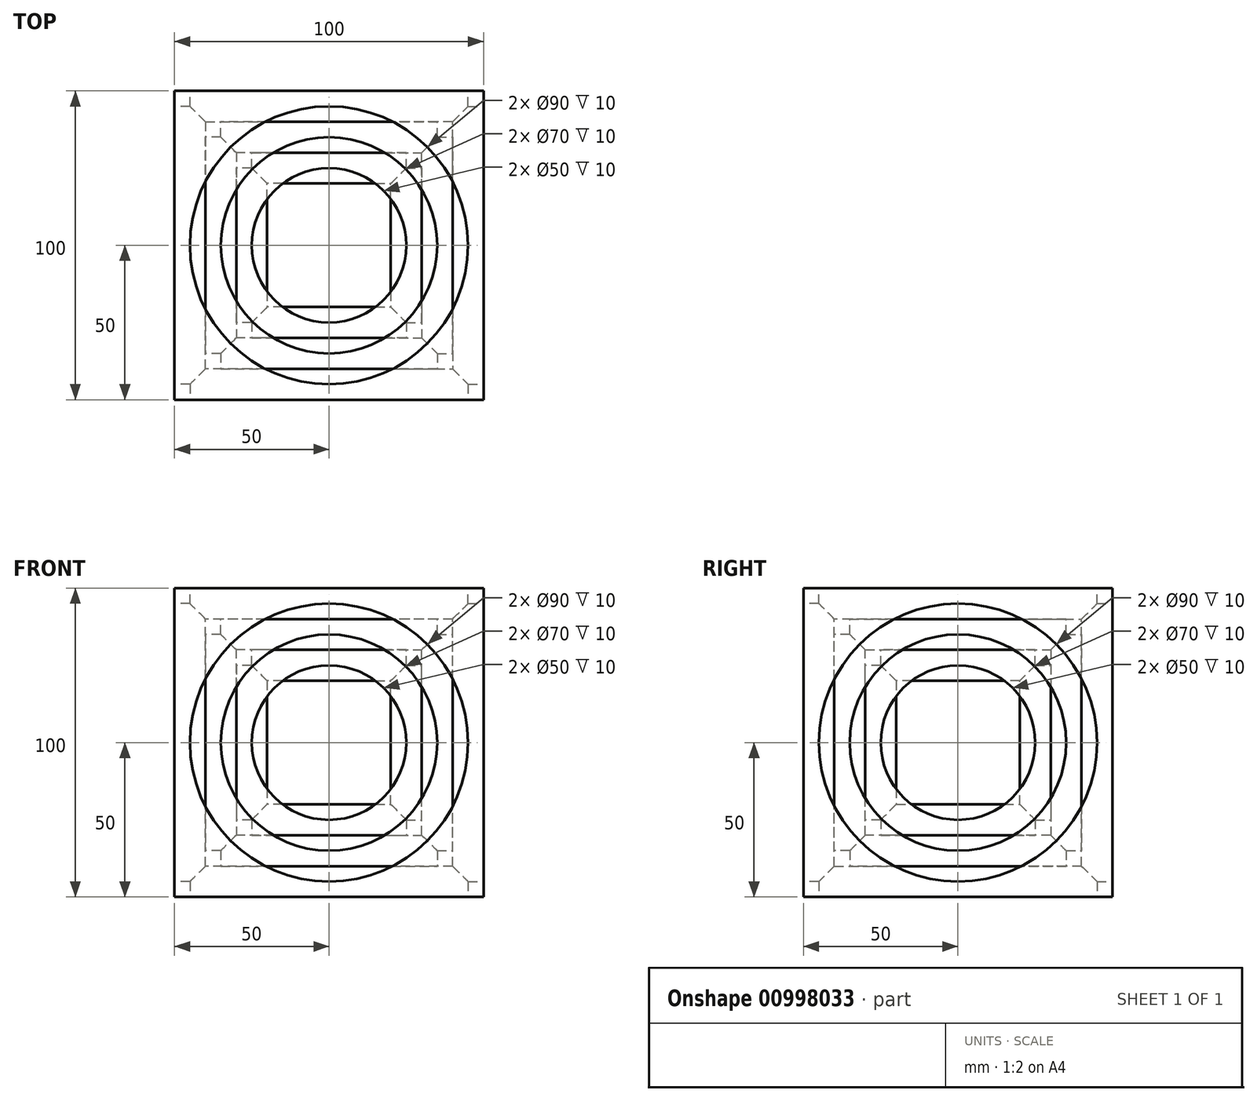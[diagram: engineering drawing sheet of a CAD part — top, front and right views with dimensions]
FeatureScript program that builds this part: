
annotation { "Feature Type Name" : "Feature", "Feature Type Description" : "" }
export const myFeature = defineFeature(function(context is Context, id is Id, definition is map)
    precondition{}
    {
        {
            assignVariable(context, id + "F0", {"name" : "W", "anyValue" : 100});
        }
        {
            assignVariable(context, id + "F1", {"name" : "S", "anyValue" : 10});
        }
        {
            var Q0;
            Q0=qCreatedBy(makeId("Top.planeOp"),FACE);
            var sketch = newSketch(context, id + "F2", { "sketchPlane" : qUnion([Q0])});
            skLineSegment(sketch, "E0.bottom", {"start": v(50, -50) * mm, "end": v(-50, -50) * mm});
            skLineSegment(sketch, "E0.top", {"start": v(50, 50) * mm, "end": v(-50, 50) * mm});
            skLineSegment(sketch, "E0.left", {"start": v(50, -50) * mm, "end": v(50, 50) * mm});
            skLineSegment(sketch, "E0.right", {"start": v(-50, -50) * mm, "end": v(-50, 50) * mm});
            skPoint(sketch, "E0.middle", {"position": v(0, 0) * mm});
            skSolve(sketch);
        }
        {
            var Q0;
            Q0=makeQuery(id+"F2.imprint","IMPRINT",FACE,{"disambiguationData":[TD([[makeQuery(id+"F2.imprint","IMPRINT",EDGE,{"derivedFrom":sQuery(id+"F2.wireOp",EDGE,"E0.bottom")}),-1.0]])]});
            extrude(context, id + "F3", {"entities" : qUnion([Q0]), "depth" : (getVariable(context, 'W') / 2) * mm, "offsetDistance" : 25 * mm, "hasSecondDirection" : true, "secondDirectionOppositeDirection" : true, "secondDirectionDepth" : (getVariable(context, 'W') / 2) * mm});
        }
        {
            var Q0;
            Q0=qCreatedBy(makeId("Front.planeOp"),FACE);
            cPlane(context, id + "F4", {"entities" : qUnion([Q0]), "cplaneType" : CPlaneType.OFFSET, "offset" : (getVariable(context, 'W') / 2) * mm, "width" : 150 * mm, "height" : 150 * mm});
        }
        {
            var Q0;
            Q0=qCreatedBy(id+"F4.planeOp",FACE);
            var sketch = newSketch(context, id + "F5", { "sketchPlane" : qUnion([Q0])});
            skCircle(sketch, "E1", {"center": v(0, 0) * mm, "radius": 45 * mm});
            skSolve(sketch);
        }
        {
            var Q0;
            Q0=makeQuery(id+"F5.imprint","IMPRINT",FACE,{"disambiguationData":[TD([[makeQuery(id+"F5.imprint","IMPRINT",EDGE,{"derivedFrom":sQuery(id+"F5.wireOp",EDGE,"E1")}),1.0]])]});
            extrude(context, id + "F6", {"entities" : qUnion([Q0]), "operationType" : NewBodyOperationType.REMOVE, "oppositeDirection" : true, "depth" : (getVariable(context, 'S')) * mm, "offsetDistance" : 25 * mm});
        }
        {
            var Q0;
            Q0=qCreatedBy(makeId("Right.planeOp"),FACE);
            cPlane(context, id + "F7", {"entities" : qUnion([Q0]), "cplaneType" : CPlaneType.OFFSET, "offset" : (getVariable(context, 'W') / 2) * mm, "width" : 150 * mm, "height" : 150 * mm});
        }
        {
            var Q0;
            Q0=qCreatedBy(id+"F7.planeOp",FACE);
            var sketch = newSketch(context, id + "F8", { "sketchPlane" : qUnion([Q0])});
            skCircle(sketch, "E2", {"center": v(0, 0) * mm, "radius": 45 * mm});
            skSolve(sketch);
        }
        {
            var Q0;
            Q0=makeQuery(id+"F8.imprint","IMPRINT",FACE,{"disambiguationData":[TD([[makeQuery(id+"F8.imprint","IMPRINT",EDGE,{"derivedFrom":sQuery(id+"F8.wireOp",EDGE,"E2")}),1.0]])]});
            extrude(context, id + "F9", {"entities" : qUnion([Q0]), "operationType" : NewBodyOperationType.REMOVE, "oppositeDirection" : true, "depth" : (getVariable(context, 'S')) * mm, "offsetDistance" : 25 * mm});
        }
        {
            var Q0;
            Q0=qCreatedBy(makeId("Top.planeOp"),FACE);
            cPlane(context, id + "F10", {"entities" : qUnion([Q0]), "cplaneType" : CPlaneType.OFFSET, "offset" : (getVariable(context, 'W') / 2) * mm, "width" : 150 * mm, "height" : 150 * mm});
        }
        {
            var Q0;
            Q0=qCreatedBy(id+"F10.planeOp",FACE);
            var sketch = newSketch(context, id + "F11", { "sketchPlane" : qUnion([Q0])});
            skCircle(sketch, "E3", {"center": v(0, 0) * mm, "radius": 45 * mm});
            skSolve(sketch);
        }
        {
            var Q0;
            Q0=makeQuery(id+"F11.imprint","IMPRINT",FACE,{"disambiguationData":[TD([[makeQuery(id+"F11.imprint","IMPRINT",EDGE,{"derivedFrom":sQuery(id+"F11.wireOp",EDGE,"E3")}),1.0]])]});
            extrude(context, id + "F12", {"entities" : qUnion([Q0]), "operationType" : NewBodyOperationType.REMOVE, "oppositeDirection" : true, "depth" : (getVariable(context, 'S')) * mm, "offsetDistance" : 25 * mm});
        }
        {
            var Q0;
            Q0=qCreatedBy(makeId("Top.planeOp"),FACE);
            cPlane(context, id + "F13", {"entities" : qUnion([Q0]), "cplaneType" : CPlaneType.OFFSET, "offset" : (getVariable(context, 'W') / 2) * mm, "oppositeDirection" : true, "width" : 150 * mm, "height" : 150 * mm});
        }
        {
            var Q0;
            Q0=qCreatedBy(id+"F13.planeOp",FACE);
            var sketch = newSketch(context, id + "F14", { "sketchPlane" : qUnion([Q0])});
            skCircle(sketch, "E4", {"center": v(0, 0) * mm, "radius": 45 * mm});
            skSolve(sketch);
        }
        {
            var Q0;
            Q0 = qSketchRegion(id + "F14", true);
            extrude(context, id + "F15", {"entities" : qUnion([Q0]), "operationType" : NewBodyOperationType.REMOVE, "oppositeDirection" : true, "depth" : (-getVariable(context, 'S')) * mm, "offsetDistance" : 25 * mm});
        }
        {
            var Q0;
            Q0=qCreatedBy(makeId("Front.planeOp"),FACE);
            cPlane(context, id + "F16", {"entities" : qUnion([Q0]), "cplaneType" : CPlaneType.OFFSET, "offset" : (getVariable(context, 'W') / 2) * mm, "oppositeDirection" : true, "width" : 150 * mm, "height" : 150 * mm});
        }
        {
            var Q0;
            Q0=qCreatedBy(id+"F16.planeOp",FACE);
            var sketch = newSketch(context, id + "F17", { "sketchPlane" : qUnion([Q0])});
            skCircle(sketch, "E5", {"center": v(0, 0) * mm, "radius": 45 * mm});
            skSolve(sketch);
        }
        {
            var Q0;
            Q0=makeQuery(id+"F17.imprint","IMPRINT",FACE,{"disambiguationData":[TD([[makeQuery(id+"F17.imprint","IMPRINT",EDGE,{"derivedFrom":sQuery(id+"F17.wireOp",EDGE,"E5")}),1.0]])]});
            extrude(context, id + "F18", {"entities" : qUnion([Q0]), "operationType" : NewBodyOperationType.REMOVE, "oppositeDirection" : true, "depth" : (-getVariable(context, 'S')) * mm, "offsetDistance" : 25 * mm});
        }
        {
            var Q0;
            Q0=qCreatedBy(makeId("Right.planeOp"),FACE);
            cPlane(context, id + "F19", {"entities" : qUnion([Q0]), "cplaneType" : CPlaneType.OFFSET, "offset" : (getVariable(context, 'W') / 2) * mm, "oppositeDirection" : true, "width" : 150 * mm, "height" : 150 * mm});
        }
        {
            var Q0;
            Q0=qCreatedBy(id+"F19.planeOp",FACE);
            var sketch = newSketch(context, id + "F20", { "sketchPlane" : qUnion([Q0])});
            skCircle(sketch, "E6", {"center": v(0, 0) * mm, "radius": 45 * mm});
            skSolve(sketch);
        }
        {
            var Q0;
            Q0=makeQuery(id+"F20.imprint","IMPRINT",FACE,{"disambiguationData":[TD([[makeQuery(id+"F20.imprint","IMPRINT",EDGE,{"derivedFrom":sQuery(id+"F20.wireOp",EDGE,"E6")}),1.0]])]});
            extrude(context, id + "F21", {"entities" : qUnion([Q0]), "operationType" : NewBodyOperationType.REMOVE, "oppositeDirection" : true, "depth" : (-getVariable(context, 'S')) * mm, "offsetDistance" : 25 * mm});
        }
        {
            var Q0;
            Q0=makeQuery(id+"F21.boolean.opBoolean","COPY",FACE,{"derivedFrom":makeQuery(id+"F21.opExtrude","CAP_FACE",FACE,{"disambiguationData":[OSD([sQuery(id+"F20.wireOp",EDGE,"E6")])],"isStart":false})});
            var sketch = newSketch(context, id + "F22", { "sketchPlane" : qUnion([Q0])});
            skLineSegment(sketch, "E7", {"start": v(0, 40) * mm, "end": v(0, -40) * mm, "construction": true});
            skCircle(sketch, "E8", {"center": v(0, 0) * mm, "radius": 35 * mm});
            skSolve(sketch);
        }
        {
            var Q0;
            Q0=makeQuery(id+"F22.imprint","IMPRINT",FACE,{"disambiguationData":[TD([[makeQuery(id+"F22.imprint","IMPRINT",EDGE,{"derivedFrom":sQuery(id+"F22.wireOp",EDGE,"E8")}),1.0]])]});
            extrude(context, id + "F23", {"entities" : qUnion([Q0]), "operationType" : NewBodyOperationType.REMOVE, "oppositeDirection" : true, "depth" : (getVariable(context, 'S')) * mm, "offsetDistance" : 25 * mm});
        }
        {
            var Q0;
            Q0=makeQuery(id+"F6.boolean.opBoolean","COPY",FACE,{"derivedFrom":makeQuery(id+"F6.opExtrude","CAP_FACE",FACE,{"disambiguationData":[OSD([sQuery(id+"F5.wireOp",EDGE,"E1")])],"isStart":false})});
            var sketch = newSketch(context, id + "F24", { "sketchPlane" : qUnion([Q0])});
            skLineSegment(sketch, "E9", {"start": v(0, 24.49) * mm, "end": v(0, -24.49) * mm, "construction": true});
            skCircle(sketch, "E10", {"center": v(0, 0) * mm, "radius": 35 * mm});
            skSolve(sketch);
        }
        {
            var Q0;
            Q0=makeQuery(id+"F24.imprint","IMPRINT",FACE,{"disambiguationData":[TD([[makeQuery(id+"F24.imprint","IMPRINT",EDGE,{"derivedFrom":sQuery(id+"F24.wireOp",EDGE,"E10")}),1.0]])]});
            extrude(context, id + "F25", {"entities" : qUnion([Q0]), "operationType" : NewBodyOperationType.REMOVE, "oppositeDirection" : true, "depth" : (getVariable(context, 'S')) * mm, "offsetDistance" : 25 * mm});
        }
        {
            var Q0;
            Q0=makeQuery(id+"F12.boolean.opBoolean","COPY",FACE,{"derivedFrom":makeQuery(id+"F12.opExtrude","CAP_FACE",FACE,{"disambiguationData":[OSD([sQuery(id+"F11.wireOp",EDGE,"E3")])],"isStart":false})});
            var sketch = newSketch(context, id + "F26", { "sketchPlane" : qUnion([Q0])});
            skLineSegment(sketch, "E11", {"start": v(0, 24.49) * mm, "end": v(0, -24.49) * mm, "construction": true});
            skCircle(sketch, "E12", {"center": v(0, 0) * mm, "radius": 35 * mm});
            skSolve(sketch);
        }
        {
            var Q0;
            Q0=makeQuery(id+"F26.imprint","IMPRINT",FACE,{"disambiguationData":[TD([[makeQuery(id+"F26.imprint","IMPRINT",EDGE,{"derivedFrom":sQuery(id+"F26.wireOp",EDGE,"E12")}),1.0]])]});
            extrude(context, id + "F27", {"entities" : qUnion([Q0]), "operationType" : NewBodyOperationType.REMOVE, "oppositeDirection" : true, "depth" : (getVariable(context, 'S')) * mm, "offsetDistance" : 25 * mm});
        }
        {
            var Q0;
            Q0=makeQuery(id+"F18.boolean.opBoolean","COPY",FACE,{"derivedFrom":makeQuery(id+"F18.opExtrude","CAP_FACE",FACE,{"disambiguationData":[OSD([sQuery(id+"F17.wireOp",EDGE,"E5")])],"isStart":false})});
            var sketch = newSketch(context, id + "F28", { "sketchPlane" : qUnion([Q0])});
            skLineSegment(sketch, "E13", {"start": v(0, 24.49) * mm, "end": v(0, -24.49) * mm, "construction": true});
            skCircle(sketch, "E14", {"center": v(0, 0) * mm, "radius": 35 * mm});
            skSolve(sketch);
        }
        {
            var Q0;
            Q0=makeQuery(id+"F28.imprint","IMPRINT",FACE,{"disambiguationData":[TD([[makeQuery(id+"F28.imprint","IMPRINT",EDGE,{"derivedFrom":sQuery(id+"F28.wireOp",EDGE,"E14")}),1.0]])]});
            extrude(context, id + "F29", {"entities" : qUnion([Q0]), "operationType" : NewBodyOperationType.REMOVE, "oppositeDirection" : true, "depth" : (getVariable(context, 'S')) * mm, "offsetDistance" : 25 * mm});
        }
        {
            var Q0;
            Q0=makeQuery(id+"F15.boolean.opBoolean","COPY",FACE,{"derivedFrom":makeQuery(id+"F15.opExtrude","CAP_FACE",FACE,{"disambiguationData":[OSD([sQuery(id+"F14.wireOp",EDGE,"E4")])],"isStart":false})});
            var sketch = newSketch(context, id + "F30", { "sketchPlane" : qUnion([Q0])});
            skLineSegment(sketch, "E15", {"start": v(0, 24.49) * mm, "end": v(0, -24.49) * mm, "construction": true});
            skCircle(sketch, "E16", {"center": v(0, 0) * mm, "radius": 35 * mm});
            skSolve(sketch);
        }
        {
            var Q0;
            Q0=makeQuery(id+"F30.imprint","IMPRINT",FACE,{"disambiguationData":[TD([[makeQuery(id+"F30.imprint","IMPRINT",EDGE,{"derivedFrom":sQuery(id+"F30.wireOp",EDGE,"E16")}),1.0]])]});
            extrude(context, id + "F31", {"entities" : qUnion([Q0]), "operationType" : NewBodyOperationType.REMOVE, "oppositeDirection" : true, "depth" : (getVariable(context, 'S')) * mm, "offsetDistance" : 25 * mm});
        }
        {
            var Q0;
            Q0=makeQuery(id+"F9.boolean.opBoolean","COPY",FACE,{"derivedFrom":makeQuery(id+"F9.opExtrude","CAP_FACE",FACE,{"disambiguationData":[OSD([sQuery(id+"F8.wireOp",EDGE,"E2")])],"isStart":false})});
            var sketch = newSketch(context, id + "F32", { "sketchPlane" : qUnion([Q0])});
            skLineSegment(sketch, "E17", {"start": v(0, 24.49) * mm, "end": v(0, -24.49) * mm, "construction": true});
            skCircle(sketch, "E18", {"center": v(0, 0) * mm, "radius": 35 * mm});
            skSolve(sketch);
        }
        {
            var Q0;
            Q0=makeQuery(id+"F32.imprint","IMPRINT",FACE,{"disambiguationData":[TD([[makeQuery(id+"F32.imprint","IMPRINT",EDGE,{"derivedFrom":sQuery(id+"F32.wireOp",EDGE,"E18")}),1.0]])]});
            extrude(context, id + "F33", {"entities" : qUnion([Q0]), "operationType" : NewBodyOperationType.REMOVE, "oppositeDirection" : true, "depth" : (getVariable(context, 'S')) * mm, "offsetDistance" : 25 * mm});
        }
        {
            var Q0;
            Q0=makeQuery(id+"F25.boolean.opBoolean","COPY",FACE,{"derivedFrom":makeQuery(id+"F25.opExtrude","CAP_FACE",FACE,{"disambiguationData":[OSD([sQuery(id+"F24.wireOp",EDGE,"E10")])],"isStart":false})});
            var sketch = newSketch(context, id + "F34", { "sketchPlane" : qUnion([Q0])});
            skLineSegment(sketch, "E19", {"start": v(0, 15.6) * mm, "end": v(0, -15.6) * mm, "construction": true});
            skCircle(sketch, "E20", {"center": v(0, 0) * mm, "radius": 25 * mm});
            skSolve(sketch);
        }
        {
            var Q0;
            Q0=makeQuery(id+"F34.imprint","IMPRINT",FACE,{"disambiguationData":[TD([[makeQuery(id+"F34.imprint","IMPRINT",EDGE,{"derivedFrom":sQuery(id+"F34.wireOp",EDGE,"E20")}),1.0]])]});
            extrude(context, id + "F35", {"entities" : qUnion([Q0]), "operationType" : NewBodyOperationType.REMOVE, "oppositeDirection" : true, "depth" : (getVariable(context, 'S')) * mm, "offsetDistance" : 25 * mm});
        }
        {
            var Q0;
            Q0=makeQuery(id+"F31.boolean.opBoolean","COPY",FACE,{"derivedFrom":makeQuery(id+"F31.opExtrude","CAP_FACE",FACE,{"disambiguationData":[OSD([sQuery(id+"F30.wireOp",EDGE,"E16")])],"isStart":false})});
            var sketch = newSketch(context, id + "F36", { "sketchPlane" : qUnion([Q0])});
            skLineSegment(sketch, "E21", {"start": v(0, 15.6) * mm, "end": v(0, -15.6) * mm, "construction": true});
            skCircle(sketch, "E22", {"center": v(0, 0) * mm, "radius": 25 * mm});
            skSolve(sketch);
        }
        {
            var Q0;
            Q0=makeQuery(id+"F36.imprint","IMPRINT",FACE,{"disambiguationData":[TD([[makeQuery(id+"F36.imprint","IMPRINT",EDGE,{"derivedFrom":sQuery(id+"F36.wireOp",EDGE,"E22")}),1.0]])]});
            extrude(context, id + "F37", {"entities" : qUnion([Q0]), "operationType" : NewBodyOperationType.REMOVE, "oppositeDirection" : true, "depth" : (getVariable(context, 'S')) * mm, "offsetDistance" : 25 * mm});
        }
        {
            var Q0;
            Q0=makeQuery(id+"F29.boolean.opBoolean","COPY",FACE,{"derivedFrom":makeQuery(id+"F29.opExtrude","CAP_FACE",FACE,{"disambiguationData":[OSD([sQuery(id+"F28.wireOp",EDGE,"E14")])],"isStart":false})});
            var sketch = newSketch(context, id + "F38", { "sketchPlane" : qUnion([Q0])});
            skLineSegment(sketch, "E23", {"start": v(0, 15.6) * mm, "end": v(0, -15.6) * mm, "construction": true});
            skCircle(sketch, "E24", {"center": v(0, 0) * mm, "radius": 25 * mm});
            skSolve(sketch);
        }
        {
            var Q0;
            Q0=makeQuery(id+"F38.imprint","IMPRINT",FACE,{"disambiguationData":[TD([[makeQuery(id+"F38.imprint","IMPRINT",EDGE,{"derivedFrom":sQuery(id+"F38.wireOp",EDGE,"E24")}),1.0]])]});
            extrude(context, id + "F39", {"entities" : qUnion([Q0]), "operationType" : NewBodyOperationType.REMOVE, "oppositeDirection" : true, "depth" : (getVariable(context, 'S')) * mm, "offsetDistance" : 25 * mm});
        }
        {
            var Q0;
            Q0=makeQuery(id+"F27.boolean.opBoolean","COPY",FACE,{"derivedFrom":makeQuery(id+"F27.opExtrude","CAP_FACE",FACE,{"disambiguationData":[OSD([sQuery(id+"F26.wireOp",EDGE,"E12")])],"isStart":false})});
            var sketch = newSketch(context, id + "F40", { "sketchPlane" : qUnion([Q0])});
            skLineSegment(sketch, "E25", {"start": v(0, 15.6) * mm, "end": v(0, -15.6) * mm, "construction": true});
            skCircle(sketch, "E26", {"center": v(0, 0) * mm, "radius": 25 * mm});
            skSolve(sketch);
        }
        {
            var Q0;
            Q0=makeQuery(id+"F40.imprint","IMPRINT",FACE,{"disambiguationData":[TD([[makeQuery(id+"F40.imprint","IMPRINT",EDGE,{"derivedFrom":sQuery(id+"F40.wireOp",EDGE,"E26")}),1.0]])]});
            extrude(context, id + "F41", {"entities" : qUnion([Q0]), "operationType" : NewBodyOperationType.REMOVE, "oppositeDirection" : true, "depth" : (getVariable(context, 'S')) * mm, "offsetDistance" : 25 * mm});
        }
        {
            var Q0;
            Q0=makeQuery(id+"F33.boolean.opBoolean","COPY",FACE,{"derivedFrom":makeQuery(id+"F33.opExtrude","CAP_FACE",FACE,{"disambiguationData":[OSD([sQuery(id+"F32.wireOp",EDGE,"E18")])],"isStart":false})});
            var sketch = newSketch(context, id + "F42", { "sketchPlane" : qUnion([Q0])});
            skLineSegment(sketch, "E27", {"start": v(0, 15.6) * mm, "end": v(0, -15.6) * mm, "construction": true});
            skCircle(sketch, "E28", {"center": v(0, 0) * mm, "radius": 25 * mm});
            skSolve(sketch);
        }
        {
            var Q0;
            Q0=makeQuery(id+"F42.imprint","IMPRINT",FACE,{"disambiguationData":[TD([[makeQuery(id+"F42.imprint","IMPRINT",EDGE,{"derivedFrom":sQuery(id+"F42.wireOp",EDGE,"E28")}),1.0]])]});
            extrude(context, id + "F43", {"entities" : qUnion([Q0]), "operationType" : NewBodyOperationType.REMOVE, "oppositeDirection" : true, "depth" : (getVariable(context, 'S')) * mm, "offsetDistance" : 25 * mm});
        }
        {
            var Q0;
            Q0=makeQuery(id+"F23.boolean.opBoolean","COPY",FACE,{"derivedFrom":makeQuery(id+"F23.opExtrude","CAP_FACE",FACE,{"disambiguationData":[OSD([sQuery(id+"F22.wireOp",EDGE,"E8")])],"isStart":false})});
            var sketch = newSketch(context, id + "F44", { "sketchPlane" : qUnion([Q0])});
            skLineSegment(sketch, "E29", {"start": v(0, 15.6) * mm, "end": v(0, -15.6) * mm, "construction": true});
            skCircle(sketch, "E30", {"center": v(0, 0) * mm, "radius": 25 * mm});
            skSolve(sketch);
        }
        {
            var Q0;
            Q0=makeQuery(id+"F44.imprint","IMPRINT",FACE,{"disambiguationData":[TD([[makeQuery(id+"F44.imprint","IMPRINT",EDGE,{"derivedFrom":sQuery(id+"F44.wireOp",EDGE,"E30")}),1.0]])]});
            extrude(context, id + "F45", {"entities" : qUnion([Q0]), "operationType" : NewBodyOperationType.REMOVE, "oppositeDirection" : true, "depth" : (getVariable(context, 'S')) * mm, "offsetDistance" : 25 * mm});
        }
    });
